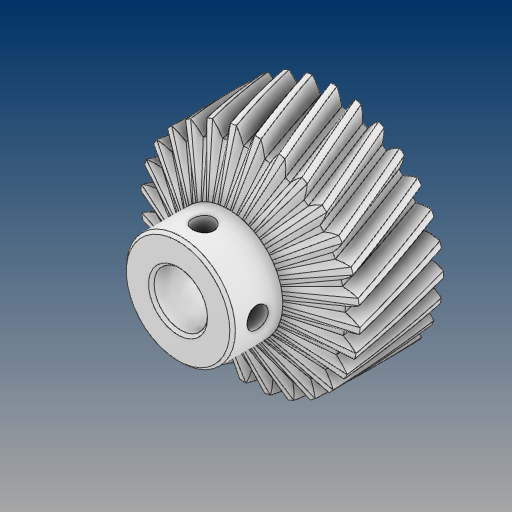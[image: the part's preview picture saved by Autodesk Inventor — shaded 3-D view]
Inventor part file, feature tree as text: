
AUTODESK INVENTOR PART (.ipt)
format: ipt  version: 2021 (Build 250183000, 183)  size: 1,046,016 bytes
history: native  units: mm (DEFAULTED — no unit token found)
features: sketch x6, extrude x5, plane x4, other x4, chamfer x2, pattern_circular x1, loft x1, projected_geometry x1
ambient origin geometry x8: Origin, YZ Plane, XZ Plane, XY Plane, X Axis, Y Axis, Z Axis, Center Point
bodies: Solid1 (feature_tree)
feature tree (24):
  extrude  "Extrusion1"  Depth=15.0mm TaperAngle=0.0deg
  plane  "Work Plane2"
  plane  "Work Plane8"
  plane  "Work Plane9"
  other  "Spur Gear"
  sketch  "Sketch3"  dims[d16=45.0mm d17=0.0mm d34=1.121997mm]
  extrude  "Extrusion2"  Depth=10.0mm TaperAngle=0.0deg
  extrude  "Extrusion3"  Depth=1.121997mm TaperAngle=0.0deg
  chamfer  "Chamfer1"  Distance=45.0mm
  chamfer  "Chamfer2"  [1 undecoded]
  extrude  "Extrusion4"  Depth=9.6mm
  pattern_circular  "Circular Pattern1"  [2 undecoded]
  plane  "Work Plane11"
  loft  "Loft1"
  extrude  "Extrusion5"  Depth=13.0mm TaperAngle=0.0deg
  sketch  "Sketch1"  dims[d0=39.395974mm d1=15.0mm d2=0.0mm]
  sketch  "Sketch2"  dims[d3=37.246222mm d4=10.0mm d5=0.0mm]
  other  "Srf1"
  sketch  "Sketch4"  dims[d39=0.0mm]
  projected_geometry  "Projected Loop1"
  sketch  "Sketch5"  dims[d41=0.0mm]
  other  "Edges1"
  sketch  "Sketch6"  dims[d43=45.0mm d46=45.0mm d47=0.0mm d48=0.0mm d49=9.6mm d50=5.0mm d51=69.5mm d52=0.0mm d53=13.0mm d54=0.0mm d55=0.5mm d56=2.0mm d57=45.0deg d58=0.5mm d59=2.0mm d60=45.0deg d62=4.0mm d63=3.8mm d64=10.0mm d65=0.0mm d66=20.0mm d67=90.0deg d69=4.0mm d70=0.0mm d71=90.0deg d72=0.0mm d73=90.0deg d74=46.25mm d75=0.0mm]
  other  "Pitch Diameter"
note: 3 required parameter values undecoded (feature->parameter linkage not recoverable at this tier; creation-order binding heuristic only, values carry confidence <= 0.55)
